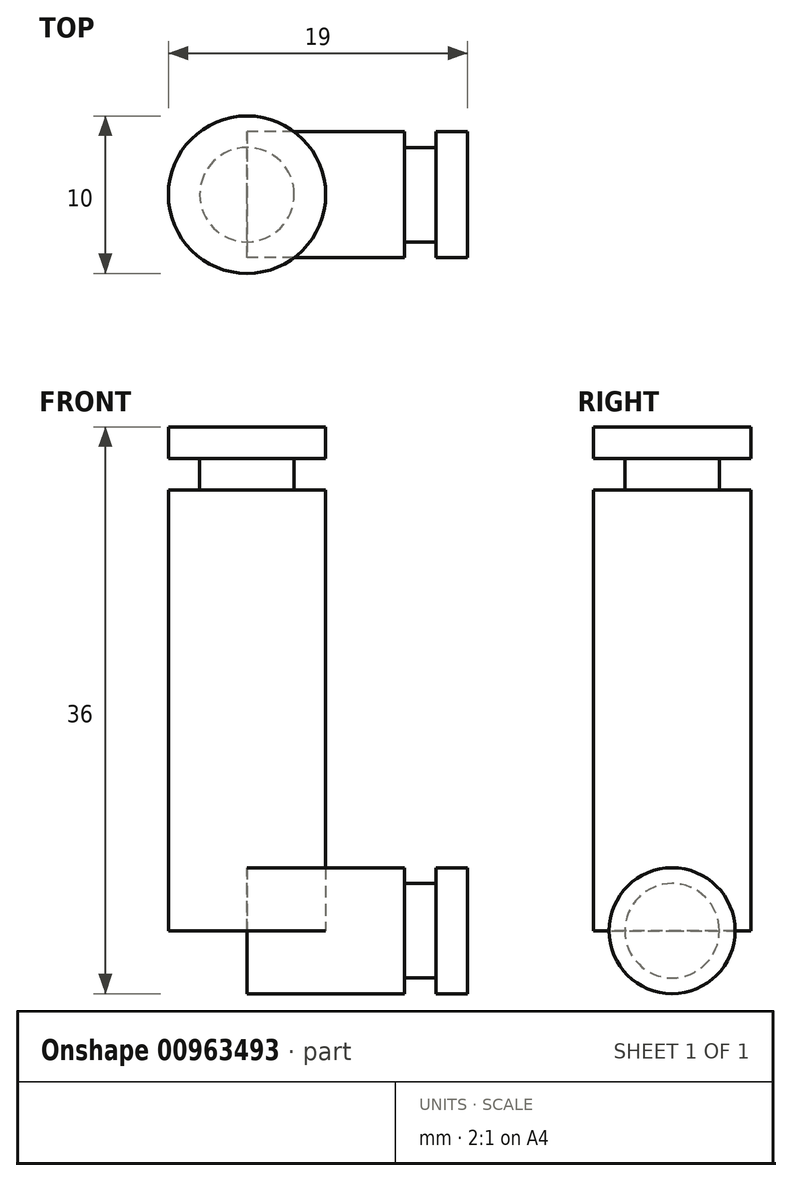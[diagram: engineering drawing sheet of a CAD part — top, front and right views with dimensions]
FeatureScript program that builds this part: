
annotation { "Feature Type Name" : "Feature", "Feature Type Description" : "" }
export const myFeature = defineFeature(function(context is Context, id is Id, definition is map)
    precondition{}
    {
        {
            var Q0;
            Q0=qCreatedBy(makeId("Front.planeOp"),FACE);
            var sketch = newSketch(context, id + "F0", { "sketchPlane" : qUnion([Q0])});
            skLineSegment(sketch, "E0.bottom", {"start": v(0, 0) * mm, "end": v(14, 0) * mm});
            skLineSegment(sketch, "E0.top", {"start": v(0, 4) * mm, "end": v(10, 4) * mm});
            skLineSegment(sketch, "E0.left", {"start": v(0, 0) * mm, "end": v(0, 4) * mm});
            skLineSegment(sketch, "E0.right", {"start": v(14, 0) * mm, "end": v(14, 4) * mm});
            skLineSegment(sketch, "E1.top", {"start": v(10, 3) * mm, "end": v(12, 3) * mm});
            skLineSegment(sketch, "E1.left", {"start": v(10, 4) * mm, "end": v(10, 3) * mm});
            skLineSegment(sketch, "E1.right", {"start": v(12, 4) * mm, "end": v(12, 3) * mm});
            skLineSegment(sketch, "E2.trimOffspring", {"start": v(12, 4) * mm, "end": v(14, 4) * mm});
            skLineSegment(sketch, "E3", {"start": v(-9.1, 0) * mm, "end": v(16.12, 0) * mm, "construction": true});
            skSolve(sketch);
        }
        {
            var Q0;
            Q0=qSketchRegion(id+"F0",true);
            var Q1;
            Q1=sQuery(id+"F0.wireOp",EDGE,"E3");
            revolve(context, id + "F1", {"entities" : qUnion([Q0]), "axis" : qUnion([Q1]), "revolveType" : RevolveType.FULL});
        }
        {
            var Q0;
            Q0=qCreatedBy(makeId("Front.planeOp"),FACE);
            var sketch = newSketch(context, id + "F2", { "sketchPlane" : qUnion([Q0])});
            skLineSegment(sketch, "E4.bottom", {"start": v(0, 0) * mm, "end": v(-5, 0) * mm});
            skLineSegment(sketch, "E4.top", {"start": v(0, 32) * mm, "end": v(-5, 32) * mm});
            skLineSegment(sketch, "E4.left", {"start": v(0, 0) * mm, "end": v(0, 32) * mm});
            skLineSegment(sketch, "E4.right", {"start": v(-5, 0) * mm, "end": v(-5, 28) * mm});
            skLineSegment(sketch, "E5.bottom", {"start": v(-5, 30) * mm, "end": v(-3, 30) * mm});
            skLineSegment(sketch, "E5.top", {"start": v(-5, 28) * mm, "end": v(-3, 28) * mm});
            skLineSegment(sketch, "E5.right", {"start": v(-3, 30) * mm, "end": v(-3, 28) * mm});
            skLineSegment(sketch, "E6.trimOffspring", {"start": v(-5, 30) * mm, "end": v(-5, 32) * mm});
            skLineSegment(sketch, "E7", {"start": v(0, -8.43) * mm, "end": v(0, 46.98) * mm, "construction": true});
            skSolve(sketch);
        }
        {
            var Q0;
            Q0=qSketchRegion(id+"F2",true);
            var Q1;
            Q1=sQuery(id+"F2.wireOp",EDGE,"E7");
            revolve(context, id + "F3", {"entities" : qUnion([Q0]), "axis" : qUnion([Q1]), "revolveType" : RevolveType.FULL});
        }
    });
